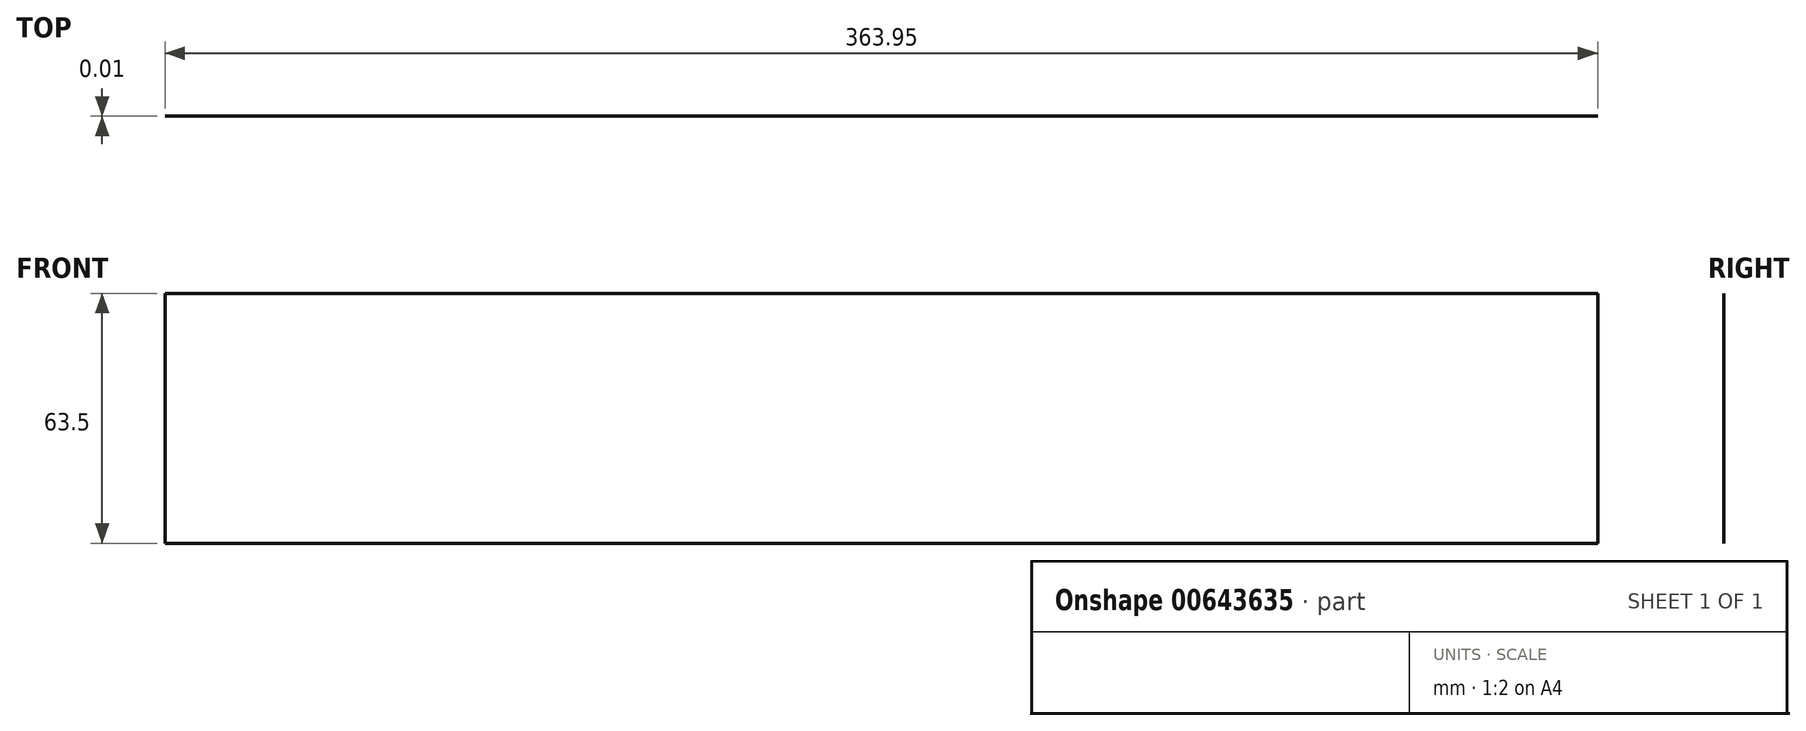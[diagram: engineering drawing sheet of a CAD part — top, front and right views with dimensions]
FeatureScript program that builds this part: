
annotation { "Feature Type Name" : "Feature", "Feature Type Description" : "" }
export const myFeature = defineFeature(function(context is Context, id is Id, definition is map)
    precondition{}
    {
        {
            var Q0;
            Q0=qCreatedBy(makeId("Front.planeOp"),FACE);
            var sketch = newSketch(context, id + "F0", { "sketchPlane" : qUnion([Q0])});
            skLineSegment(sketch, "E0.bottom", {"start": v(0, 0) * mm, "end": v(363.95, 0) * mm});
            skLineSegment(sketch, "E0.top", {"start": v(0, 63.5) * mm, "end": v(363.95, 63.5) * mm});
            skLineSegment(sketch, "E0.left", {"start": v(0, 0) * mm, "end": v(0, 63.5) * mm});
            skLineSegment(sketch, "E0.right", {"start": v(363.95, 0) * mm, "end": v(363.95, 63.5) * mm});
            skSolve(sketch);
        }
        {
            var Q0;
            Q0=makeQuery(id+"F0.imprint","IMPRINT",FACE,{"disambiguationData":[TD([[makeQuery(id+"F0.imprint","IMPRINT",EDGE,{"derivedFrom":sQuery(id+"F0.wireOp",EDGE,"E0.bottom")}),1.0]])]});
            extrude(context, id + "F1", {"entities" : qUnion([Q0]), "oppositeDirection" : true, "depth" : 3 / 203.2 * mm, "offsetDistance" : 25.4 * mm});
        }
        {
            var Q0;
            Q0=makeQuery(id+"F1.opExtrude","SWEPT_FACE",FACE,{"disambiguationData":[OSD([sQuery(id+"F0.wireOp",EDGE,"E0.bottom")])]});
            var sketch = newSketch(context, id + "F2", { "sketchPlane" : qUnion([Q0])});
            skLineSegment(sketch, "E1", {"start": v(0, -5) * mm, "end": v(363.95, -5) * mm, "construction": true});
            skPoint(sketch, "E2", {"position": v(19.98, -5) * mm});
            skPoint(sketch, "E3", {"position": v(181.97, -5) * mm});
            skPoint(sketch, "E4", {"position": v(343.97, -5) * mm});
            skSolve(sketch);
        }
        {
            var Q0;
            Q0=sQuery(id+"F2.wireOp",VERTEX,"E2");
            var Q1;
            Q1=sQuery(id+"F2.wireOp",VERTEX,"E3");
            var Q2;
            Q2=sQuery(id+"F2.wireOp",VERTEX,"E4");
            var Q3;
            Q3=sQuery(id+"F2.wireOp",VERTEX,"51501e4f-45b7-4127-b72b-e308d7c7158c");
            var Q4;
            Q4=sQuery(id+"F2.wireOp",VERTEX,"2ac52b9b-2078-49d3-80a3-9a8250e7101a");
            var Q5;
            Q5=makeQuery(id+"F1.opExtrude","SWEPT_BODY",BODY,{"disambiguationData":[OSD([sQuery(id+"F0.wireOp",EDGE,"E0.bottom"),sQuery(id+"F0.wireOp",EDGE,"E0.top"),sQuery(id+"F0.wireOp",EDGE,"E0.left"),sQuery(id+"F0.wireOp",EDGE,"E0.right")])]});
            hole(context, id + "F3", {"style" : HoleStyle.SIMPLE, "endStyle" : HoleEndStyle.BLIND, "standardTappedOrClearance" : lookupTablePath({ "standard" : "ISO", "engagement" : "75%", "pitch" : "0.7 mm", "size" : "M4", "type" : "Tapped" }), "standardBlindInLast" : lookupTablePath({ "standard" : "ISO", "engagement" : "75%", "pitch" : "0.7 mm", "size" : "M4", "type" : "Tapped" }), "holeDiameter" : 3.3 * mm, "majorDiameter" : 4 * mm, "showTappedDepth" : true, "holeDepth" : 15 * mm, "isTappedThrough" : true, "tappedDepth" : 12.9 * mm, "tapClearance" : 3, "locations" : qUnion([Q0, Q1, Q2, Q3, Q4]), "scope" : qUnion([Q5])});
        }
        {
            var Q0;
            Q0=makeQuery(id+"F1.opExtrude","CAP_EDGE",EDGE,{"disambiguationData":[OSD([sQuery(id+"F0.wireOp",EDGE,"E0.left")])],"isStart":true});
            cPoint(context, id + "F4", {"entities" : qUnion([Q0]), "parameter" : 0.5});
        }
        {
            var Q0;
            Q0=qCreatedBy(id+"F4",VERTEX);
            var Q1;
            Q1=makeQuery(id+"F1.opExtrude","SWEPT_FACE",FACE,{"disambiguationData":[OSD([sQuery(id+"F0.wireOp",EDGE,"E0.bottom")])]});
            cPlane(context, id + "F5", {"entities" : qUnion([Q0, Q1]), "cplaneType" : CPlaneType.PLANE_POINT, "offset" : 25 * mm, "width" : 150 * mm, "height" : 150 * mm});
        }
    });
